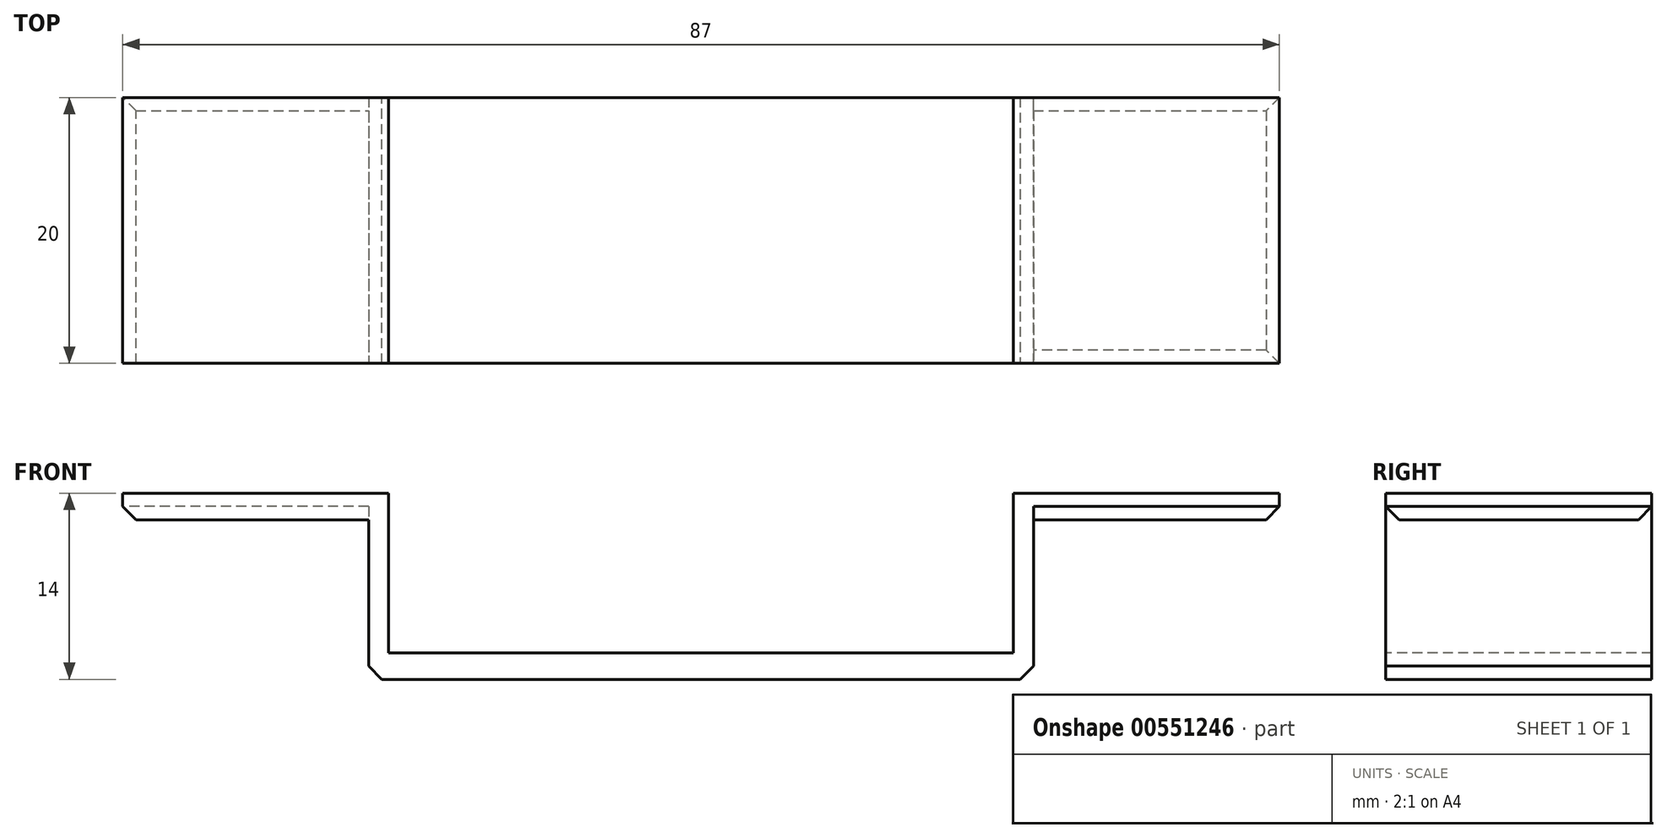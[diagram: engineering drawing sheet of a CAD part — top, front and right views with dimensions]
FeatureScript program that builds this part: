
annotation { "Feature Type Name" : "Feature", "Feature Type Description" : "" }
export const myFeature = defineFeature(function(context is Context, id is Id, definition is map)
    precondition{}
    {
        {
            var Q0;
            Q0=qCreatedBy(makeId("Top.planeOp"),FACE);
            var sketch = newSketch(context, id + "F0", { "sketchPlane" : qUnion([Q0])});
            skLineSegment(sketch, "E0.bottom", {"start": v(25, 10) * mm, "end": v(-25, 10) * mm});
            skLineSegment(sketch, "E0.top", {"start": v(25, -10) * mm, "end": v(-25, -10) * mm});
            skLineSegment(sketch, "E0.left", {"start": v(25, 10) * mm, "end": v(25, -10) * mm});
            skLineSegment(sketch, "E0.right", {"start": v(-25, 10) * mm, "end": v(-25, -10) * mm});
            skPoint(sketch, "E0.middle", {"position": v(0, 0) * mm});
            skSolve(sketch);
        }
        {
            var Q0;
            Q0 = qSketchRegion(id + "F0", true);
            extrude(context, id + "F1", {"entities" : qUnion([Q0]), "depth" : 2 * mm, "offsetDistance" : 25 * mm});
        }
        {
            var Q0;
            Q0=makeQuery(id+"F1.opExtrude","CAP_FACE",FACE,{"disambiguationData":[OSD([sQuery(id+"F0.wireOp",EDGE,"E0.bottom"),sQuery(id+"F0.wireOp",EDGE,"E0.top"),sQuery(id+"F0.wireOp",EDGE,"E0.left"),sQuery(id+"F0.wireOp",EDGE,"E0.right")])],"isStart":false});
            var sketch = newSketch(context, id + "F2", { "sketchPlane" : qUnion([Q0])});
            skLineSegment(sketch, "E1.bottom", {"start": v(-25, 10) * mm, "end": v(-23.5, 10) * mm});
            skLineSegment(sketch, "E1.top", {"start": v(-25, -10) * mm, "end": v(-23.5, -10) * mm});
            skLineSegment(sketch, "E1.left", {"start": v(-25, 10) * mm, "end": v(-25, -10) * mm});
            skLineSegment(sketch, "E1.right", {"start": v(-23.5, 10) * mm, "end": v(-23.5, -10) * mm});
            skLineSegment(sketch, "E2.MirrorCS", {"start": v(23.5, 10) * mm, "end": v(23.5, -10) * mm});
            skLineSegment(sketch, "E3.MirrorCS", {"start": v(25, 10) * mm, "end": v(25, -10) * mm});
            skLineSegment(sketch, "E4.MirrorCS", {"start": v(25, 10) * mm, "end": v(23.5, 10) * mm});
            skLineSegment(sketch, "E5.MirrorCS", {"start": v(25, -10) * mm, "end": v(23.5, -10) * mm});
            skSolve(sketch);
        }
        {
            var Q0;
            Q0 = qSketchRegion(id + "F2", true);
            extrude(context, id + "F3", {"entities" : qUnion([Q0]), "operationType" : NewBodyOperationType.ADD, "depth" : 10 * mm, "offsetDistance" : 25 * mm});
        }
        {
            var Q0;
            Q0=makeQuery(id+"F3.opExtrude","CAP_FACE",FACE,{"disambiguationData":[OSD([sQuery(id+"F2.wireOp",EDGE,"E1.bottom"),sQuery(id+"F2.wireOp",EDGE,"E1.top"),sQuery(id+"F2.wireOp",EDGE,"E1.left"),sQuery(id+"F2.wireOp",EDGE,"E1.right")])],"isStart":false});
            var sketch = newSketch(context, id + "F4", { "sketchPlane" : qUnion([Q0])});
            skPoint(sketch, "E6.oppositeSnap0", {"position": v(-24.25, -10) * mm});
            skLineSegment(sketch, "E6.bottom", {"start": v(-23.5, 10) * mm, "end": v(-43.5, 10) * mm});
            skLineSegment(sketch, "E6.top", {"start": v(-23.5, -10) * mm, "end": v(-43.5, -10) * mm});
            skLineSegment(sketch, "E6.left", {"start": v(-23.5, 10) * mm, "end": v(-23.5, -10) * mm});
            skLineSegment(sketch, "E6.right", {"start": v(-43.5, 10) * mm, "end": v(-43.5, -10) * mm});
            skLineSegment(sketch, "E7.MirrorCS", {"start": v(23.5, 10) * mm, "end": v(43.5, 10) * mm});
            skLineSegment(sketch, "E8.MirrorCS", {"start": v(43.5, 10) * mm, "end": v(43.5, -10) * mm});
            skLineSegment(sketch, "E9.MirrorCS", {"start": v(23.5, -10) * mm, "end": v(43.5, -10) * mm});
            skLineSegment(sketch, "E10.MirrorCS", {"start": v(23.5, 10) * mm, "end": v(23.5, -10) * mm});
            skSolve(sketch);
        }
        {
            var Q0;
            Q0 = qSketchRegion(id + "F4", true);
            extrude(context, id + "F5", {"entities" : qUnion([Q0]), "operationType" : NewBodyOperationType.ADD, "depth" : 2 * mm, "offsetDistance" : 25 * mm});
        }
        {
            var Q0;
            Q0=makeQuery(id+"F1.opExtrude","CAP_EDGE",EDGE,{"disambiguationData":[OSD([sQuery(id+"F0.wireOp",EDGE,"E0.right")])],"isStart":true});
            var Q1;
            Q1=makeQuery(id+"F1.opExtrude","CAP_EDGE",EDGE,{"disambiguationData":[OSD([sQuery(id+"F0.wireOp",EDGE,"E0.left")])],"isStart":true});
            var Q2;
            Q2=makeQuery(id+"F5.opExtrude","CAP_EDGE",EDGE,{"disambiguationData":[OSD([sQuery(id+"F4.wireOp",EDGE,"E6.right")])],"isStart":true});
            var Q3;
            Q3=makeQuery(id+"F5.opExtrude","CAP_EDGE",EDGE,{"disambiguationData":[OSD([sQuery(id+"F4.wireOp",EDGE,"E8.MirrorCS")])],"isStart":true});
            var Q4;
            Q4=makeQuery(id+"F5.opExtrude","CAP_EDGE",EDGE,{"disambiguationData":[OSD([sQuery(id+"F4.wireOp",EDGE,"E9.MirrorCS")])],"isStart":true});
            var Q5;
            Q5=makeQuery(id+"F5.opExtrude","CAP_EDGE",EDGE,{"disambiguationData":[OSD([sQuery(id+"F4.wireOp",EDGE,"E7.MirrorCS")])],"isStart":true});
            var Q6;
            Q6=makeQuery(id+"F5.opExtrude","CAP_EDGE",EDGE,{"disambiguationData":[OSD([sQuery(id+"F4.wireOp",EDGE,"E6.bottom")])],"isStart":true});
            chamfer(context, id + "F6", {"entities" : qUnion([Q0, Q1, Q2, Q3, Q4, Q5, Q6]), "width" : 1 * mm});
        }
    });
